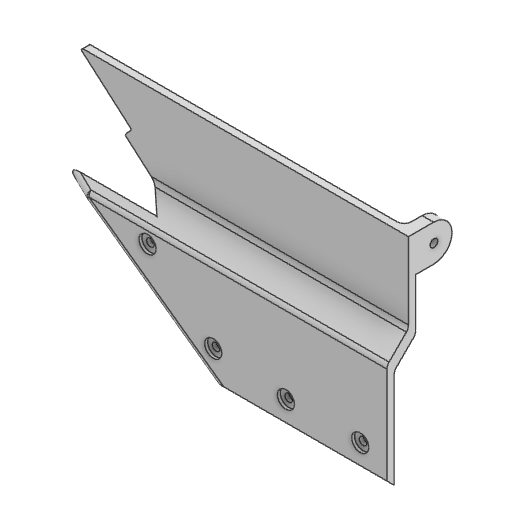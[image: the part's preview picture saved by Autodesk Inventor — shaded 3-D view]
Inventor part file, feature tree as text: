
AUTODESK INVENTOR PART (.ipt)
format: ipt  version: 2025 (Build 290162000, 162)  size: 272,896 bytes
history: native  units: mm
features: reference x13, other x11, extrude x9, sketch x9, projected_geometry x8, fillet x6, chamfer x3, thicken_offset x1
ambient origin geometry x8: Origin, YZ Plane, XZ Plane, XY Plane, X Axis, Y Axis, Z Axis, Center Point
bodies: Solid1 (feature_tree)
feature tree (60):
  extrude  "Extrusion1"  TaperAngle=0.0deg  [1 undecoded]
  extrude  "Extrusion2"  Depth=5.0mm TaperAngle=0.0deg
  extrude  "Extrusion3"  Depth=15.0mm TaperAngle=45.0deg
  extrude  "Extrusion4"  Depth=5.0mm
  chamfer  "Chamfer1"  [1 undecoded]
  chamfer  "Chamfer2"  Distance=25.4mm
  chamfer  "Chamfer3"  Distance=8.0mm
  fillet  "Fillet1"  Radius=25.4mm
  fillet  "Fillet2"  Radius=5.5mm
  extrude  "Extrusion5"  Depth=25.4mm TaperAngle=0.0deg
  thicken_offset  "Thicken1"
  fillet  "Fillet3"  Radius=5.0mm
  extrude  "Extrusion6"  Depth=12.9mm
  extrude  "Extrusion7"  Depth=5.0mm
  fillet  "Fillet4"  Radius=5.5mm
  fillet  "Fillet5"  Radius=5.5mm
  fillet  "Fillet6"  Radius=5.5mm
  extrude  "Extrusion8"  TaperAngle=0.0deg  [1 undecoded]
  extrude  "Extrusion9"  Depth=2.0mm
  sketch  "Sketch1"  dims[d0=5.0mm d1=0.0mm d3=0.0mm d4=0.0mm]
  reference  "Reference1"
  reference  "Reference2"
  reference  "Reference3"
  reference  "Reference4"
  sketch  "Sketch2"  dims[d5=15.0mm d6=0.0mm d7=5.0mm d8=0.0mm]
  projected_geometry  "Projected Loop1"
  sketch  "Sketch3"  dims[d9=15.0mm d10=2.0mm d11=45.0deg d12=15.0mm d13=2.0mm d14=45.0deg]
  projected_geometry  "Projected Loop2"
  reference  "Reference5"
  sketch  "Sketch4"  dims[d15=5.0mm d16=2.0mm d17=45.0deg d18=5.0mm]
  projected_geometry  "Projected Loop3"
  projected_geometry  "Projected Loop4"
  reference  "Reference6"
  reference  "Reference7"
  reference  "Reference8"
  sketch  "Sketch5"  dims[d19=5.0mm]
  reference  "Reference9"
  projected_geometry  "Projected Loop5"
  reference  "Reference10"
  sketch  "Sketch6"  dims[d20=1.0mm d21=0.0mm d22=0.0mm]
  projected_geometry  "Projected Loop6"
  sketch  "Sketch7"  dims[d23=1.0mm]
  projected_geometry  "Projected Loop7"
  sketch  "Sketch8"  dims[d24=1.0mm]
  reference  "Reference11"
  reference  "Reference12"
  reference  "Reference13"
  sketch  "Sketch9"  dims[d25=1.0mm d26=25.4mm d27=8.0mm d28=25.4mm d29=0.0mm d30=5.5mm d31=25.4mm d32=0.0mm d33=5.0mm d34=12.9mm d35=5.0mm d36=5.5mm d37=5.5mm d38=5.5mm d39=0.0mm d40=0.0mm d41=5.5mm d42=12.0mm d43=12.0mm d44=12.0mm d45=12.0mm d46=2.0mm d47=0.0mm]
  projected_geometry  "Projected Loop8"
  other  "<userpath>\Desktop\puppycat\woodhouseMK1.iam"
  other  "woodhouseMK1.iam"
  other  "trackBase:1"
  other  "6pt9inStrut:1"
  other  "lowerSkidPlateRear:1"
  other  "upperFrontSkidPlate:1"
  other  "6pt9inStrut:2"
  other  "trackBase:2"
  other  "frontUndercarriageBracket:1"
  other  "lowerSkidPlate:1"
  other  "lowerUndercarriageBracket:1"
note: 3 required parameter values undecoded (feature->parameter linkage not recoverable at this tier; creation-order binding heuristic only, values carry confidence <= 0.55)
